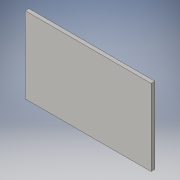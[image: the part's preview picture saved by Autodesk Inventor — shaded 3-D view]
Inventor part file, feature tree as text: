
AUTODESK INVENTOR PART (.ipt)
format: ipt  version: 2016 (Build 200138000, 138)  size: 87,552 bytes
history: native  units: in
note: dims shown in document units (in); Inventor stores cm internally (conversion verified against a paired STEP export)
features: extrude x1, sketch x1
ambient origin geometry x8: Origin, YZ Plane, XZ Plane, XY Plane, X Axis, Y Axis, Z Axis, Center Point
bodies: Solid1 (feature_tree)
feature tree (2):
  extrude  "Extrusion1"  [1 undecoded]
  sketch  "Sketch1"  dims[d3=0.0in]
note: 1 required parameter value undecoded (feature->parameter linkage not recoverable at this tier; creation-order binding heuristic only, values carry confidence <= 0.55)
